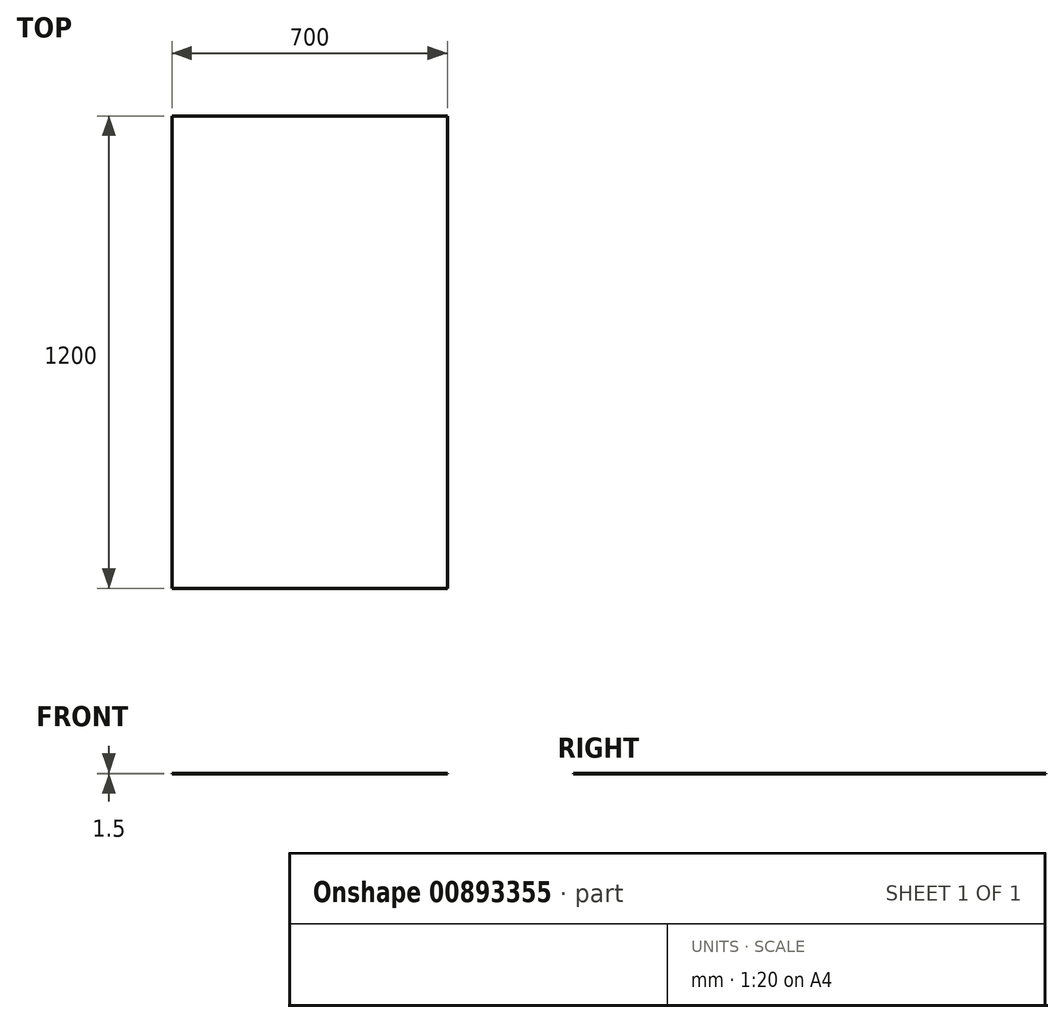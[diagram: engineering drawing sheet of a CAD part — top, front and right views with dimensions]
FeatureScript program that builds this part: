
annotation { "Feature Type Name" : "Feature", "Feature Type Description" : "" }
export const myFeature = defineFeature(function(context is Context, id is Id, definition is map)
    precondition{}
    {
        {
            var Q0;
            Q0=qCreatedBy(makeId("Top.planeOp"),FACE);
            var sketch = newSketch(context, id + "F0", { "sketchPlane" : qUnion([Q0])});
            skLineSegment(sketch, "E0.bottom", {"start": v(350, 600) * mm, "end": v(-350, 600) * mm});
            skLineSegment(sketch, "E0.top", {"start": v(350, -600) * mm, "end": v(-350, -600) * mm});
            skLineSegment(sketch, "E0.left", {"start": v(350, 600) * mm, "end": v(350, -600) * mm});
            skLineSegment(sketch, "E0.right", {"start": v(-350, 600) * mm, "end": v(-350, -600) * mm});
            skPoint(sketch, "E0.middle", {"position": v(0, 0) * mm});
            skSolve(sketch);
        }
        {
            var Q0;
            Q0=makeQuery(id+"F0.imprint","IMPRINT",FACE,{"disambiguationData":[TD([[makeQuery(id+"F0.imprint","IMPRINT",EDGE,{"derivedFrom":sQuery(id+"F0.wireOp",EDGE,"E0.bottom")}),1.0]])]});
            extrude(context, id + "F1", {"entities" : qUnion([Q0]), "depth" : 1.5 * mm, "offsetDistance" : 25 * mm});
        }
    });
